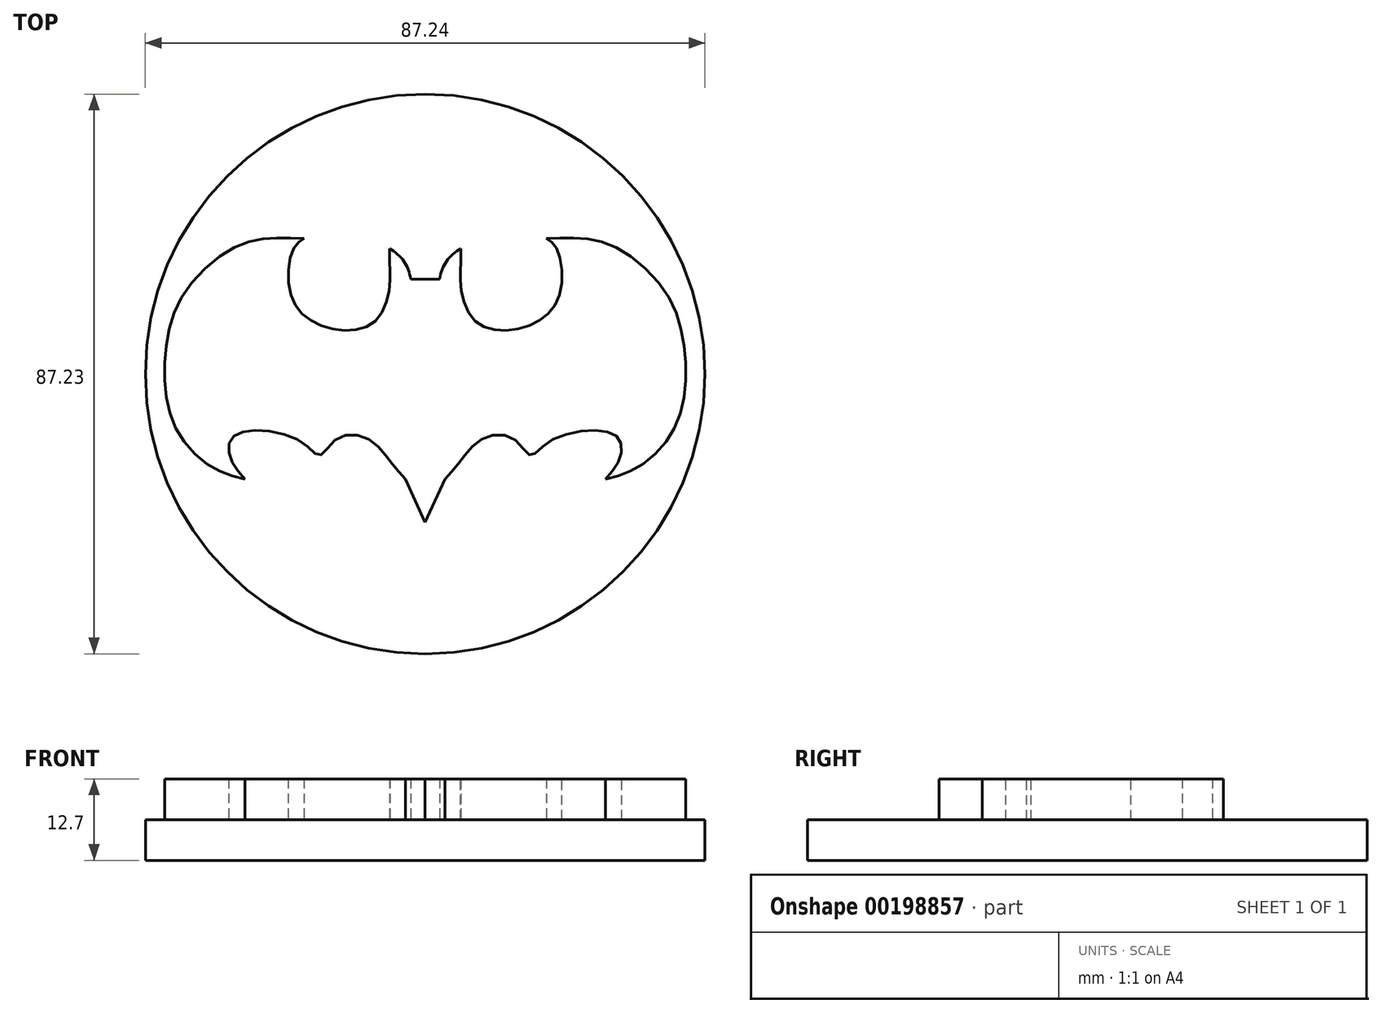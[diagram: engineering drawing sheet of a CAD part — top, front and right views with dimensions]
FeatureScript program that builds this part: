
annotation { "Feature Type Name" : "Feature", "Feature Type Description" : "" }
export const myFeature = defineFeature(function(context is Context, id is Id, definition is map)
    precondition{}
    {
        {
            var Q0;
            Q0=qCreatedBy(makeId("Top.planeOp"),FACE);
            var sketch = newSketch(context, id + "F0", { "sketchPlane" : qUnion([Q0])});
            skLineSegment(sketch, "E0", {"start": v(0, 37.9) * mm, "end": v(-2.28, 37.9) * mm});
            skArc(sketch, "E1", {"start": v(-2.28, 37.9) * mm, "mid": v(-3.33, 40.66) * mm, "end": v(-5.56, 42.61) * mm});
            skPoint(sketch, "E2.1.internal.snap0", {"position": v(-3.33, 40.66) * mm});
            skFitSpline(sketch, "E2", {"points": [v(-5.56, 42.61) * mm, v(-5.56, 40.66) * mm, v(-5.56, 36.67) * mm, v(-7.6, 31.54) * mm, v(-12.53, 29.9) * mm, v(-18.27, 31.75) * mm, v(-21.14, 36.26) * mm, v(-20.53, 42.61) * mm, v(-18.89, 44.26) * mm], "startDerivative": vector(-0.51, -21.73) * mm, "endDerivative": vector(19.87, 12.83) * mm});
            skFitSpline(sketch, "E3", {"points": [v(-18.89, 44.26) * mm, v(-24.22, 44.26) * mm, v(-30.16, 42.61) * mm, v(-37.34, 36.05) * mm, v(-40.21, 28.47) * mm, v(-40.42, 20.06) * mm, v(-37.96, 13.09) * mm, v(-32.83, 8.37) * mm, v(-28.11, 6.73) * mm], "startDerivative": vector(-48.89, 1.89) * mm, "endDerivative": vector(44.6, -11.01) * mm});
            skFitSpline(sketch, "E4", {"points": [v(-28.11, 6.73) * mm, v(-30.37, 10) * mm, v(-30.16, 13.09) * mm, v(-26.06, 14.32) * mm, v(-18.89, 12.27) * mm, v(-16.42, 10.42) * mm, v(-13.96, 12.88) * mm, v(-9.04, 13.09) * mm, v(-5.56, 9.6) * mm, v(-3.1, 6.73) * mm], "startDerivative": vector(-25.42, 28.78) * mm, "endDerivative": vector(23.18, -25.55) * mm});
            skLineSegment(sketch, "E5", {"start": v(-3.1, 6.73) * mm, "end": v(0, 0) * mm});
            skLineSegment(sketch, "E6", {"start": v(0, 37.9) * mm, "end": v(0, 0) * mm});
            skFitSpline(sketch, "E7.MirrorCS", {"points": [v(5.56, 42.61) * mm, v(5.56, 40.66) * mm, v(5.56, 36.67) * mm, v(7.6, 31.54) * mm, v(12.53, 29.9) * mm, v(18.27, 31.75) * mm, v(21.14, 36.26) * mm, v(20.53, 42.61) * mm, v(18.89, 44.26) * mm], "startDerivative": vector(0.51, -21.73) * mm, "endDerivative": vector(-19.87, 12.83) * mm});
            skPoint(sketch, "E8.MirrorP", {"position": v(3.33, 40.66) * mm});
            skFitSpline(sketch, "E9.MirrorCS", {"points": [v(18.89, 44.26) * mm, v(24.22, 44.26) * mm, v(30.16, 42.61) * mm, v(37.34, 36.05) * mm, v(40.21, 28.47) * mm, v(40.42, 20.06) * mm, v(37.96, 13.09) * mm, v(32.83, 8.37) * mm, v(28.11, 6.73) * mm], "startDerivative": vector(48.89, 1.89) * mm, "endDerivative": vector(-44.6, -11.01) * mm});
            skFitSpline(sketch, "E10.MirrorCS", {"points": [v(28.11, 6.73) * mm, v(30.37, 10) * mm, v(30.16, 13.09) * mm, v(26.06, 14.32) * mm, v(18.89, 12.27) * mm, v(16.42, 10.42) * mm, v(13.96, 12.88) * mm, v(9.04, 13.09) * mm, v(5.56, 9.6) * mm, v(3.1, 6.73) * mm], "startDerivative": vector(25.42, 28.78) * mm, "endDerivative": vector(-23.18, -25.55) * mm});
            skLineSegment(sketch, "E11.MirrorCS", {"start": v(3.1, 6.73) * mm, "end": v(0, 0) * mm});
            skArc(sketch, "E12.MirrorCS", {"start": v(2.28, 37.9) * mm, "mid": v(3.33, 40.66) * mm, "end": v(5.56, 42.61) * mm});
            skLineSegment(sketch, "E13.MirrorCS", {"start": v(0, 37.9) * mm, "end": v(2.28, 37.9) * mm});
            skSolve(sketch);
        }
        {
            var Q0;
            Q0=makeQuery(id+"F0.imprint","IMPRINT",FACE,{"disambiguationData":[TD([[makeQuery(id+"F0.imprint","IMPRINT",EDGE,{"derivedFrom":sQuery(id+"F0.wireOp",EDGE,"E0")}),1.0]])]});
            var Q1;
            Q1=makeQuery(id+"F0.imprint","IMPRINT",FACE,{"disambiguationData":[TD([[makeQuery(id+"F0.imprint","IMPRINT",EDGE,{"derivedFrom":sQuery(id+"F0.wireOp",EDGE,"E6")}),1.0]])]});
            extrude(context, id + "F1", {"entities" : qUnion([Q0, Q1]), "depth" : 12.7 * mm});
        }
        {
            var Q0;
            Q0=qCreatedBy(makeId("Top.planeOp"),FACE);
            var sketch = newSketch(context, id + "F2", { "sketchPlane" : qUnion([Q0])});
            skCircle(sketch, "E14", {"center": v(0, 23.1) * mm, "radius": 43.62 * mm});
            skSolve(sketch);
        }
        {
            var Q0;
            Q0=makeQuery(id+"F2.imprint","IMPRINT",FACE,{"disambiguationData":[TD([[makeQuery(id+"F2.imprint","IMPRINT",EDGE,{"derivedFrom":sQuery(id+"F2.wireOp",EDGE,"E14")}),1.0]])]});
            extrude(context, id + "F3", {"entities" : qUnion([Q0]), "operationType" : NewBodyOperationType.ADD, "depth" : 6.35 * mm});
        }
    });
